# Revit family: Colt
name_source: partatom
category: Lighting Fixtures
revit_build: Autodesk Revit 2013 (Build: 20120221_2030(x64)
units: mm (PartAtom-declared; Revit-internal decimal feet)

## types (1)
- Colt
    Apparent Load = 0 VA
    Default Elevation = 48 "
    Description = Colt LED Floodlight
    Glass = Hubbell - Glass
    Hood = Yes
    Lamp = LED
    Load Classification = Lighting
    Manufacturer = Hubbell Outdoor Lighting
    Manufacturer Fax = 941-751-5535
    Model = COLT
    Photometric = Web : BUL-1L3K-U Wide
    Pivot Angle = 120.00°
    Power factor = 1
    Product Documentation Link = http://cdn.hubbelloutdoor.com
    Product Material = Hubbell - Dark Bronze Textured
    Product Page URL = http://www.hubbelloutdoor.com
    URL = http://www.hubbelloutdoor.com
    Voltage = 120 V
    Watt = 21 W
    Wattage Comments = 21W
    zz Angle 1 = 120.00°

## geometry (parser evidence)
native form markers: Blend x6, Sweep x6
no freeform markers — native parametric forms only
